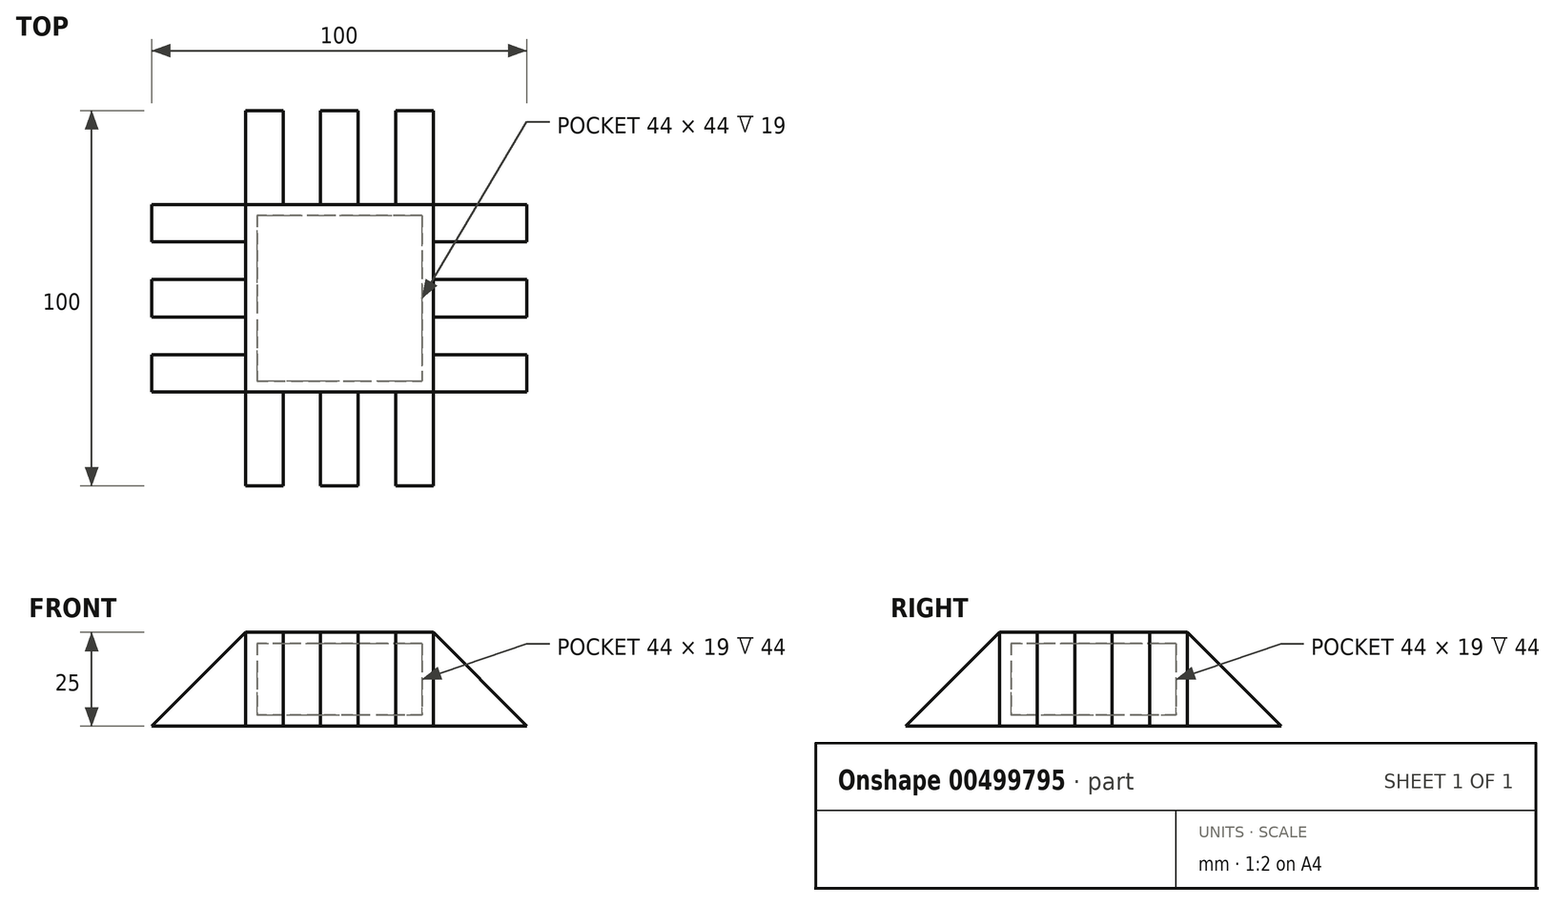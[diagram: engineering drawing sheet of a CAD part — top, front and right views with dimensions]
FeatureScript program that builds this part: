
annotation { "Feature Type Name" : "Feature", "Feature Type Description" : "" }
export const myFeature = defineFeature(function(context is Context, id is Id, definition is map)
    precondition{}
    {
        {
            var Q0;
            Q0=qCreatedBy(makeId("Top.planeOp"),FACE);
            var sketch = newSketch(context, id + "F0", { "sketchPlane" : qUnion([Q0])});
            skLineSegment(sketch, "E0", {"start": v(25, 25) * mm, "end": v(-25, 25) * mm});
            skLineSegment(sketch, "E1", {"start": v(-25, 25) * mm, "end": v(-25, -25) * mm});
            skLineSegment(sketch, "E2", {"start": v(-25, -25) * mm, "end": v(25, -25) * mm});
            skLineSegment(sketch, "E3", {"start": v(25, 25) * mm, "end": v(25, -25) * mm});
            skSolve(sketch);
        }
        {
            var Q0;
            Q0=qSketchRegion(id+"F0",true);
            extrude(context, id + "F1", {"entities" : qUnion([Q0]), "depth" : 25 * mm});
        }
        {
            var Q0;
            Q0=makeQuery(id+"F1.opExtrude","SWEPT_FACE",FACE,{"disambiguationData":[OSD([sQuery(id+"F0.wireOp",EDGE,"E0")])]});
            var Q1;
            Q1=makeQuery(id+"F1.opExtrude","CAP_FACE",FACE,{"disambiguationData":[OSD([sQuery(id+"F0.wireOp",EDGE,"E0"),sQuery(id+"F0.wireOp",EDGE,"E1"),sQuery(id+"F0.wireOp",EDGE,"E2"),sQuery(id+"F0.wireOp",EDGE,"E3")])],"isStart":false});
            var Q2;
            Q2=makeQuery(id+"F1.opExtrude","SWEPT_FACE",FACE,{"disambiguationData":[OSD([sQuery(id+"F0.wireOp",EDGE,"E3")])]});
            var Q3;
            Q3=makeQuery(id+"F1.opExtrude","SWEPT_FACE",FACE,{"disambiguationData":[OSD([sQuery(id+"F0.wireOp",EDGE,"E1")])]});
            var Q4;
            Q4=makeQuery(id+"F1.opExtrude","CAP_FACE",FACE,{"disambiguationData":[OSD([sQuery(id+"F0.wireOp",EDGE,"E0"),sQuery(id+"F0.wireOp",EDGE,"E1"),sQuery(id+"F0.wireOp",EDGE,"E2"),sQuery(id+"F0.wireOp",EDGE,"E3")])],"isStart":true});
            var Q5;
            Q5=makeQuery(id+"F1.opExtrude","SWEPT_FACE",FACE,{"disambiguationData":[OSD([sQuery(id+"F0.wireOp",EDGE,"E2")])]});
            var Q6;
            Q6=makeQuery(id+"F1.opExtrude","SWEPT_BODY",BODY,{"disambiguationData":[OSD([sQuery(id+"F0.wireOp",EDGE,"E0"),sQuery(id+"F0.wireOp",EDGE,"E1"),sQuery(id+"F0.wireOp",EDGE,"E2"),sQuery(id+"F0.wireOp",EDGE,"E3")])]});
            shell(context, id + "F2", {"isHollow" : true, "entities" : qUnion([Q0, Q1, Q2, Q3, Q4, Q5]), "parts" : qUnion([Q6]), "thickness" : 3 * mm});
        }
        {
            var Q0;
            Q0=makeQuery(id+"F1.opExtrude","SWEPT_FACE",FACE,{"disambiguationData":[OSD([sQuery(id+"F0.wireOp",EDGE,"E3")])]});
            var sketch = newSketch(context, id + "F3", { "sketchPlane" : qUnion([Q0])});
            skLineSegment(sketch, "E4", {"start": v(-25, 0) * mm, "end": v(-25, 25) * mm});
            skLineSegment(sketch, "E5", {"start": v(-25, 25) * mm, "end": v(-15, 25) * mm});
            skLineSegment(sketch, "E6", {"start": v(-15, 25) * mm, "end": v(-15, 0) * mm});
            skLineSegment(sketch, "E7", {"start": v(-15, 0) * mm, "end": v(-25, 0) * mm});
            skLineSegment(sketch, "E8", {"start": v(-5, 25) * mm, "end": v(-5, 0) * mm});
            skLineSegment(sketch, "E9", {"start": v(-5, 0) * mm, "end": v(5, 0) * mm});
            skLineSegment(sketch, "E10", {"start": v(5, 0) * mm, "end": v(5, 25) * mm});
            skLineSegment(sketch, "E11", {"start": v(5, 25) * mm, "end": v(-5, 25) * mm});
            skLineSegment(sketch, "E12", {"start": v(-5, 25) * mm, "end": v(5, 25) * mm});
            skLineSegment(sketch, "E13", {"start": v(25, 25) * mm, "end": v(15, 25) * mm});
            skLineSegment(sketch, "E14", {"start": v(15, 25) * mm, "end": v(15, 0) * mm});
            skLineSegment(sketch, "E15", {"start": v(15, 0) * mm, "end": v(25, 0) * mm});
            skLineSegment(sketch, "E16", {"start": v(25, 0) * mm, "end": v(25, 25) * mm});
            skSolve(sketch);
        }
        {
            var Q0;
            Q0=qSketchRegion(id+"F3",true);
            extrude(context, id + "F4", {"entities" : qUnion([Q0]), "operationType" : NewBodyOperationType.ADD, "depth" : 25 * mm});
        }
        {
            var Q0;
            Q0=makeQuery(id+"F4.boolean.opBoolean","MERGE",FACE,{"derivedFrom":[makeQuery(id+"F1.opExtrude","SWEPT_FACE",FACE,{"disambiguationData":[OSD([sQuery(id+"F0.wireOp",EDGE,"E2")])]}),makeQuery(id+"F4.opExtrude","SWEPT_FACE",FACE,{"disambiguationData":[OSD([sQuery(id+"F3.wireOp",EDGE,"E4")])]})]});
            var sketch = newSketch(context, id + "F5", { "sketchPlane" : qUnion([Q0])});
            skLineSegment(sketch, "E17", {"start": v(50, 25) * mm, "end": v(25, 25) * mm});
            skLineSegment(sketch, "E18", {"start": v(25, 25) * mm, "end": v(50, 0) * mm});
            skSolve(sketch);
        }
        {
            var Q0;
            Q0=makeQuery(id+"F5.imprint","IMPRINT",FACE,{"disambiguationData":[TD([[makeQuery(id+"F5.imprint","IMPRINT",EDGE,{"derivedFrom":sQuery(id+"F5.wireOp",EDGE,"E17")}),-1.0]])]});
            extrude(context, id + "F6", {"entities" : qUnion([Q0]), "operationType" : NewBodyOperationType.REMOVE, "oppositeDirection" : true, "depth" : 50 * mm});
        }
        {
            var Q0;
            Q0=makeQuery(id+"F4.boolean.opBoolean","MERGE",FACE,{"derivedFrom":[makeQuery(id+"F1.opExtrude","SWEPT_FACE",FACE,{"disambiguationData":[OSD([sQuery(id+"F0.wireOp",EDGE,"E0")])]}),makeQuery(id+"F4.opExtrude","SWEPT_FACE",FACE,{"disambiguationData":[OSD([sQuery(id+"F3.wireOp",EDGE,"E16")])]})]});
            var sketch = newSketch(context, id + "F7", { "sketchPlane" : qUnion([Q0])});
            skLineSegment(sketch, "E19", {"start": v(-25, 0) * mm, "end": v(-25, 25) * mm});
            skLineSegment(sketch, "E20", {"start": v(-25, 25) * mm, "end": v(-15, 25) * mm});
            skLineSegment(sketch, "E21", {"start": v(-15, 25) * mm, "end": v(-15, 0) * mm});
            skLineSegment(sketch, "E22", {"start": v(-15, 0) * mm, "end": v(-25, 0) * mm});
            skLineSegment(sketch, "E23", {"start": v(-5, 25) * mm, "end": v(-5, 0) * mm});
            skLineSegment(sketch, "E24", {"start": v(-5, 0) * mm, "end": v(5, 0) * mm});
            skLineSegment(sketch, "E25", {"start": v(5, 0) * mm, "end": v(5, 25) * mm});
            skLineSegment(sketch, "E26", {"start": v(5, 25) * mm, "end": v(-5, 25) * mm});
            skLineSegment(sketch, "E27", {"start": v(-5, 25) * mm, "end": v(5, 25) * mm});
            skLineSegment(sketch, "E28", {"start": v(25, 25) * mm, "end": v(15, 25) * mm});
            skLineSegment(sketch, "E29", {"start": v(15, 25) * mm, "end": v(15, 0) * mm});
            skLineSegment(sketch, "E30", {"start": v(15, 0) * mm, "end": v(25, 0) * mm});
            skLineSegment(sketch, "E31", {"start": v(25, 0) * mm, "end": v(25, 25) * mm});
            skSolve(sketch);
        }
        {
            var Q0;
            Q0=qSketchRegion(id+"F7",true);
            extrude(context, id + "F8", {"entities" : qUnion([Q0]), "operationType" : NewBodyOperationType.ADD, "depth" : 25 * mm});
        }
        {
            var Q0;
            Q0=makeQuery(id+"F8.boolean.opBoolean","MERGE",FACE,{"derivedFrom":[makeQuery(id+"F1.opExtrude","SWEPT_FACE",FACE,{"disambiguationData":[OSD([sQuery(id+"F0.wireOp",EDGE,"E1")])]}),makeQuery(id+"F8.opExtrude","SWEPT_FACE",FACE,{"disambiguationData":[OSD([sQuery(id+"F7.wireOp",EDGE,"E31")])]})]});
            var sketch = newSketch(context, id + "F9", { "sketchPlane" : qUnion([Q0])});
            skLineSegment(sketch, "E32", {"start": v(-50, 25) * mm, "end": v(-25, 25) * mm});
            skLineSegment(sketch, "E33", {"start": v(-25, 25) * mm, "end": v(-50, 0) * mm});
            skSolve(sketch);
        }
        {
            var Q0;
            Q0=makeQuery(id+"F9.imprint","IMPRINT",FACE,{"disambiguationData":[TD([[makeQuery(id+"F9.imprint","IMPRINT",EDGE,{"derivedFrom":sQuery(id+"F9.wireOp",EDGE,"E32")}),-1.0]])]});
            extrude(context, id + "F10", {"entities" : qUnion([Q0]), "operationType" : NewBodyOperationType.REMOVE, "oppositeDirection" : true, "depth" : 50 * mm});
        }
        {
            var Q0;
            Q0=makeQuery(id+"F4.boolean.opBoolean","MERGE",FACE,{"derivedFrom":[makeQuery(id+"F1.opExtrude","SWEPT_FACE",FACE,{"disambiguationData":[OSD([sQuery(id+"F0.wireOp",EDGE,"E2")])]}),makeQuery(id+"F4.opExtrude","SWEPT_FACE",FACE,{"disambiguationData":[OSD([sQuery(id+"F3.wireOp",EDGE,"E4")])]})]});
            var sketch = newSketch(context, id + "F11", { "sketchPlane" : qUnion([Q0])});
            skLineSegment(sketch, "E34", {"start": v(-25, 0) * mm, "end": v(-25, 25) * mm});
            skLineSegment(sketch, "E35", {"start": v(-25, 25) * mm, "end": v(-15, 25) * mm});
            skLineSegment(sketch, "E36", {"start": v(-15, 25) * mm, "end": v(-15, 0) * mm});
            skLineSegment(sketch, "E37", {"start": v(-15, 0) * mm, "end": v(-25, 0) * mm});
            skLineSegment(sketch, "E38", {"start": v(-5, 25) * mm, "end": v(-5, 0) * mm});
            skLineSegment(sketch, "E39", {"start": v(-5, 0) * mm, "end": v(5, 0) * mm});
            skLineSegment(sketch, "E40", {"start": v(5, 0) * mm, "end": v(5, 25) * mm});
            skLineSegment(sketch, "E41", {"start": v(5, 25) * mm, "end": v(-5, 25) * mm});
            skLineSegment(sketch, "E42", {"start": v(-5, 25) * mm, "end": v(5, 25) * mm});
            skLineSegment(sketch, "E43", {"start": v(25, 25) * mm, "end": v(15, 25) * mm});
            skLineSegment(sketch, "E44", {"start": v(15, 25) * mm, "end": v(15, 0) * mm});
            skLineSegment(sketch, "E45", {"start": v(15, 0) * mm, "end": v(25, 0) * mm});
            skLineSegment(sketch, "E46", {"start": v(25, 0) * mm, "end": v(25, 25) * mm});
            skSolve(sketch);
        }
        {
            var Q0;
            Q0=qSketchRegion(id+"F11",true);
            extrude(context, id + "F12", {"entities" : qUnion([Q0]), "operationType" : NewBodyOperationType.ADD, "depth" : 25 * mm});
        }
        {
            var Q0;
            Q0=makeQuery(id+"F12.boolean.opBoolean","MERGE",FACE,{"derivedFrom":[makeQuery(id+"F8.boolean.opBoolean","MERGE",FACE,{"derivedFrom":[makeQuery(id+"F1.opExtrude","SWEPT_FACE",FACE,{"disambiguationData":[OSD([sQuery(id+"F0.wireOp",EDGE,"E1")])]}),makeQuery(id+"F8.opExtrude","SWEPT_FACE",FACE,{"disambiguationData":[OSD([sQuery(id+"F7.wireOp",EDGE,"E31")])]})]}),makeQuery(id+"F12.opExtrude","SWEPT_FACE",FACE,{"disambiguationData":[OSD([sQuery(id+"F11.wireOp",EDGE,"E34")])]})]});
            var sketch = newSketch(context, id + "F13", { "sketchPlane" : qUnion([Q0])});
            skLineSegment(sketch, "E47", {"start": v(50, 25) * mm, "end": v(25, 25) * mm});
            skLineSegment(sketch, "E48", {"start": v(25, 25) * mm, "end": v(50, 0) * mm});
            skSolve(sketch);
        }
        {
            var Q0;
            Q0=makeQuery(id+"F13.imprint","IMPRINT",FACE,{"disambiguationData":[TD([[makeQuery(id+"F13.imprint","IMPRINT",EDGE,{"derivedFrom":sQuery(id+"F13.wireOp",EDGE,"E47")}),-1.0]])]});
            extrude(context, id + "F14", {"entities" : qUnion([Q0]), "operationType" : NewBodyOperationType.REMOVE, "oppositeDirection" : true, "depth" : 50 * mm});
        }
        {
            var Q0;
            Q0=makeQuery(id+"F12.boolean.opBoolean","MERGE",FACE,{"derivedFrom":[makeQuery(id+"F8.boolean.opBoolean","MERGE",FACE,{"derivedFrom":[makeQuery(id+"F1.opExtrude","SWEPT_FACE",FACE,{"disambiguationData":[OSD([sQuery(id+"F0.wireOp",EDGE,"E1")])]}),makeQuery(id+"F8.opExtrude","SWEPT_FACE",FACE,{"disambiguationData":[OSD([sQuery(id+"F7.wireOp",EDGE,"E31")])]})]}),makeQuery(id+"F12.opExtrude","SWEPT_FACE",FACE,{"disambiguationData":[OSD([sQuery(id+"F11.wireOp",EDGE,"E34")])]})]});
            var sketch = newSketch(context, id + "F15", { "sketchPlane" : qUnion([Q0])});
            skLineSegment(sketch, "E49", {"start": v(-25, 0) * mm, "end": v(-25, 25) * mm});
            skLineSegment(sketch, "E50", {"start": v(-25, 25) * mm, "end": v(-15, 25) * mm});
            skLineSegment(sketch, "E51", {"start": v(-15, 25) * mm, "end": v(-15, 0) * mm});
            skLineSegment(sketch, "E52", {"start": v(-15, 0) * mm, "end": v(-25, 0) * mm});
            skLineSegment(sketch, "E53", {"start": v(-5, 25) * mm, "end": v(-5, 0) * mm});
            skLineSegment(sketch, "E54", {"start": v(-5, 0) * mm, "end": v(5, 0) * mm});
            skLineSegment(sketch, "E55", {"start": v(5, 0) * mm, "end": v(5, 25) * mm});
            skLineSegment(sketch, "E56", {"start": v(5, 25) * mm, "end": v(-5, 25) * mm});
            skLineSegment(sketch, "E57", {"start": v(-5, 25) * mm, "end": v(5, 25) * mm});
            skLineSegment(sketch, "E58", {"start": v(25, 25) * mm, "end": v(15, 25) * mm});
            skLineSegment(sketch, "E59", {"start": v(15, 25) * mm, "end": v(15, 0) * mm});
            skLineSegment(sketch, "E60", {"start": v(15, 0) * mm, "end": v(25, 0) * mm});
            skLineSegment(sketch, "E61", {"start": v(25, 0) * mm, "end": v(25, 25) * mm});
            skSolve(sketch);
        }
        {
            var Q0;
            Q0=qSketchRegion(id+"F15",true);
            extrude(context, id + "F16", {"entities" : qUnion([Q0]), "operationType" : NewBodyOperationType.ADD, "depth" : 25 * mm});
        }
        {
            var Q0;
            Q0=makeQuery(id+"F16.opExtrude","SWEPT_FACE",FACE,{"disambiguationData":[OSD([sQuery(id+"F15.wireOp",EDGE,"E49")])]});
            var sketch = newSketch(context, id + "F17", { "sketchPlane" : qUnion([Q0])});
            skLineSegment(sketch, "E62", {"start": v(25, 25) * mm, "end": v(50, 0) * mm});
            skSolve(sketch);
        }
        {
            var Q0;
            Q0=makeQuery(id+"F17.imprint","IMPRINT",FACE,{"disambiguationData":[TD([[makeQuery(id+"F17.imprint","IMPRINT",EDGE,{"derivedFrom":sQuery(id+"F17.wireOp",EDGE,"E62")}),1.0]])]});
            extrude(context, id + "F18", {"entities" : qUnion([Q0]), "operationType" : NewBodyOperationType.REMOVE, "oppositeDirection" : true, "depth" : 50 * mm});
        }
    });
